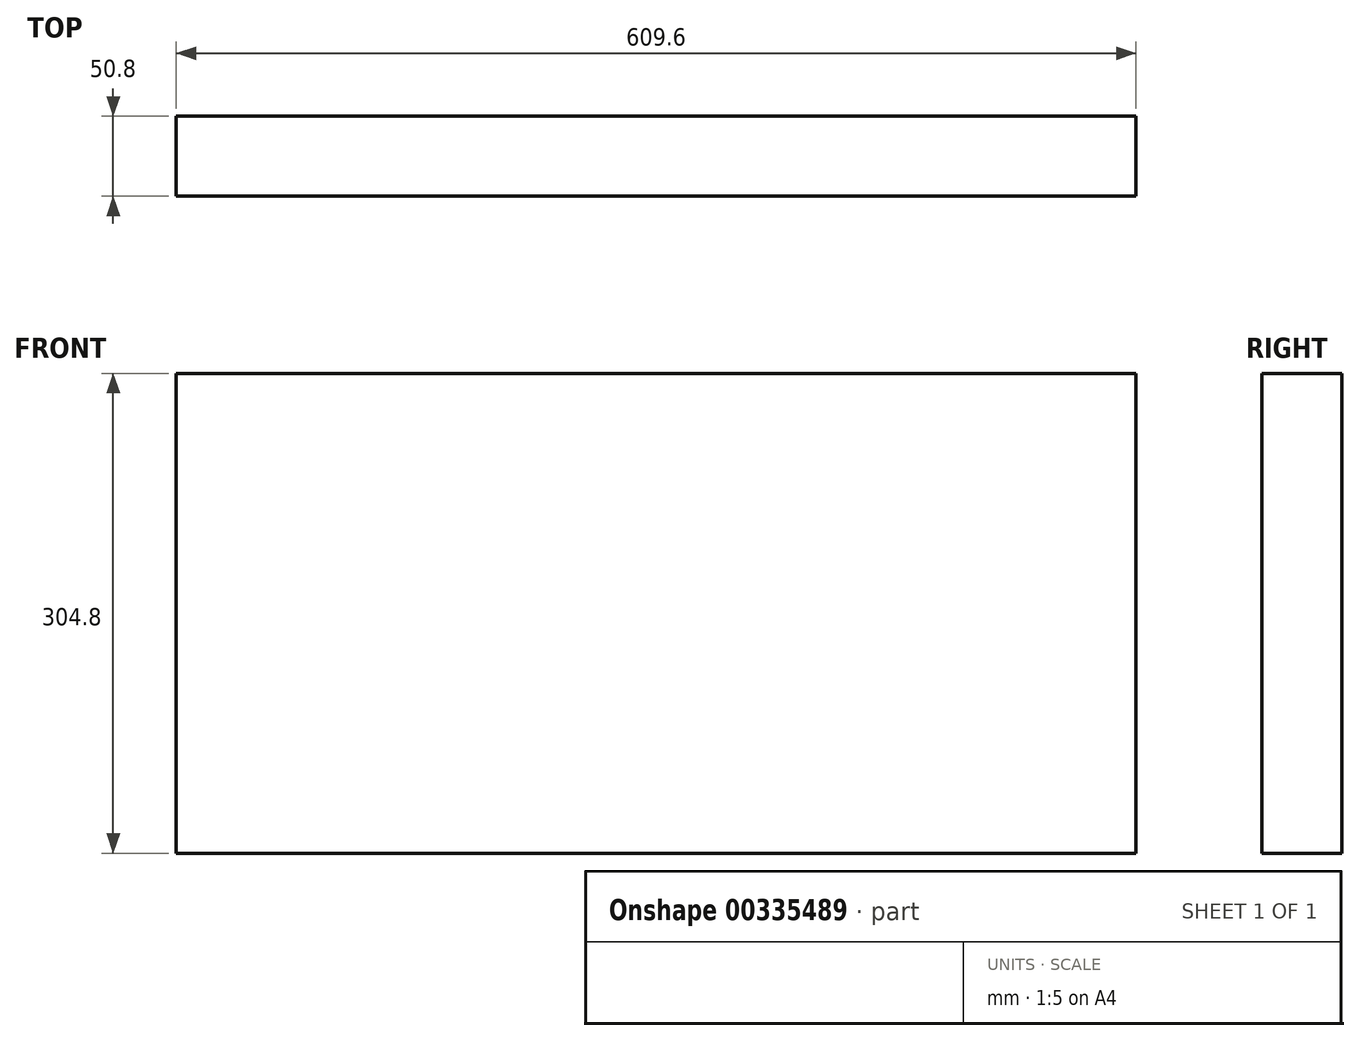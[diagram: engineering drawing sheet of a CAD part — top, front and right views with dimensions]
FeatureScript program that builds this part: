
annotation { "Feature Type Name" : "Feature", "Feature Type Description" : "" }
export const myFeature = defineFeature(function(context is Context, id is Id, definition is map)
    precondition{}
    {
        {
            var Q0;
            Q0=qCreatedBy(makeId("Front.planeOp"),FACE);
            var sketch = newSketch(context, id + "F0", { "sketchPlane" : qUnion([Q0])});
            skLineSegment(sketch, "E0.bottom", {"start": v(-152.05, 197.56) * mm, "end": v(457.55, 197.56) * mm});
            skLineSegment(sketch, "E0.top", {"start": v(-152.05, -107.24) * mm, "end": v(457.55, -107.24) * mm});
            skLineSegment(sketch, "E0.left", {"start": v(-152.05, 197.56) * mm, "end": v(-152.05, -107.24) * mm});
            skLineSegment(sketch, "E0.right", {"start": v(457.55, 197.56) * mm, "end": v(457.55, -107.24) * mm});
            skSolve(sketch);
        }
        {
            var Q0;
            Q0 = qSketchRegion(id + "F0", true);
            extrude(context, id + "F1", {"entities" : qUnion([Q0]), "depth" : 50.8 * mm});
        }
    });
